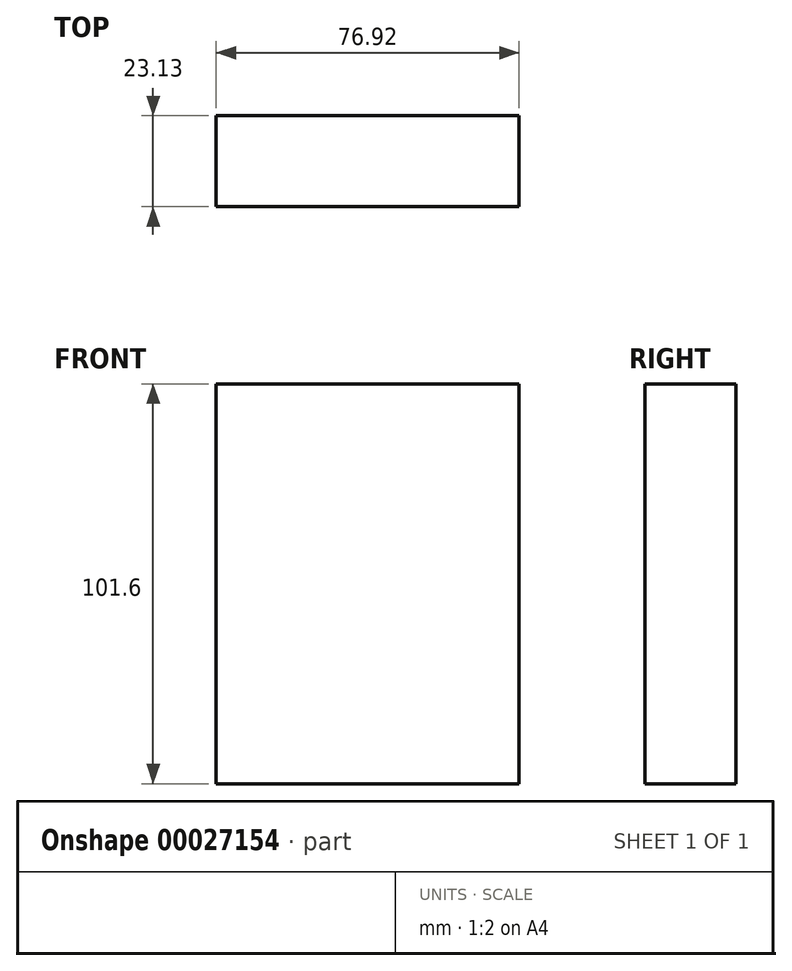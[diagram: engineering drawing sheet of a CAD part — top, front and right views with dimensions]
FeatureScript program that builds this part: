
annotation { "Feature Type Name" : "Feature", "Feature Type Description" : "" }
export const myFeature = defineFeature(function(context is Context, id is Id, definition is map)
    precondition{}
    {
        {
            var Q0;
            Q0=qCreatedBy(makeId("Top.planeOp"),FACE);
            var sketch = newSketch(context, id + "F0", { "sketchPlane" : qUnion([Q0])});
            skLineSegment(sketch, "E0.bottom", {"start": v(-39.27, 47.47) * mm, "end": v(37.65, 47.47) * mm});
            skLineSegment(sketch, "E0.top", {"start": v(-39.27, 24.34) * mm, "end": v(37.65, 24.34) * mm});
            skLineSegment(sketch, "E0.left", {"start": v(-39.27, 47.47) * mm, "end": v(-39.27, 24.34) * mm});
            skLineSegment(sketch, "E0.right", {"start": v(37.65, 47.47) * mm, "end": v(37.65, 24.34) * mm});
            skLineSegment(sketch, "E1.bottom", {"start": v(-17.75, 47.47) * mm, "end": v(19.36, 47.47) * mm});
            skLineSegment(sketch, "E1.top", {"start": v(-17.75, 64.68) * mm, "end": v(19.36, 64.68) * mm});
            skLineSegment(sketch, "E1.left", {"start": v(-17.75, 47.47) * mm, "end": v(-17.75, 64.68) * mm});
            skLineSegment(sketch, "E1.right", {"start": v(19.36, 47.47) * mm, "end": v(19.36, 64.68) * mm});
            skSolve(sketch);
        }
        {
            var Q0;
            Q0=makeQuery(id+"F0.imprint","IMPRINT",FACE,{"disambiguationData":[TD([[makeQuery(id+"F0.imprint","IMPRINT",EDGE,{"derivedFrom":sQuery(id+"F0.wireOp",EDGE,"E0.top")}),1.0]])]});
            extrude(context, id + "F1", {"entities" : qUnion([Q0]), "depth" : 101.6 * mm});
        }
        {
            var Q0;
            Q0=qCreatedBy(makeId("Top.planeOp"),FACE);
            var sketch = newSketch(context, id + "F2", { "sketchPlane" : qUnion([Q0])});
            skLineSegment(sketch, "E2.bottom", {"start": v(-57.94, -21.94) * mm, "end": v(-7.14, -21.94) * mm});
            skLineSegment(sketch, "E2.top", {"start": v(-57.94, -34.64) * mm, "end": v(-7.14, -34.64) * mm});
            skLineSegment(sketch, "E2.left", {"start": v(-57.94, -21.94) * mm, "end": v(-57.94, -34.64) * mm});
            skLineSegment(sketch, "E2.right", {"start": v(-7.14, -21.94) * mm, "end": v(-7.14, -34.64) * mm});
            skSolve(sketch);
        }
        {
            var Q0;
            Q0=sQuery(id+"F2.wireOp",EDGE,"E2.bottom");
            extrude(context, id + "F3", {"bodyType" : ToolBodyType.SURFACE, "surfaceEntities" : qUnion([Q0]), "depth" : 152.4 * mm});
        }
    });
